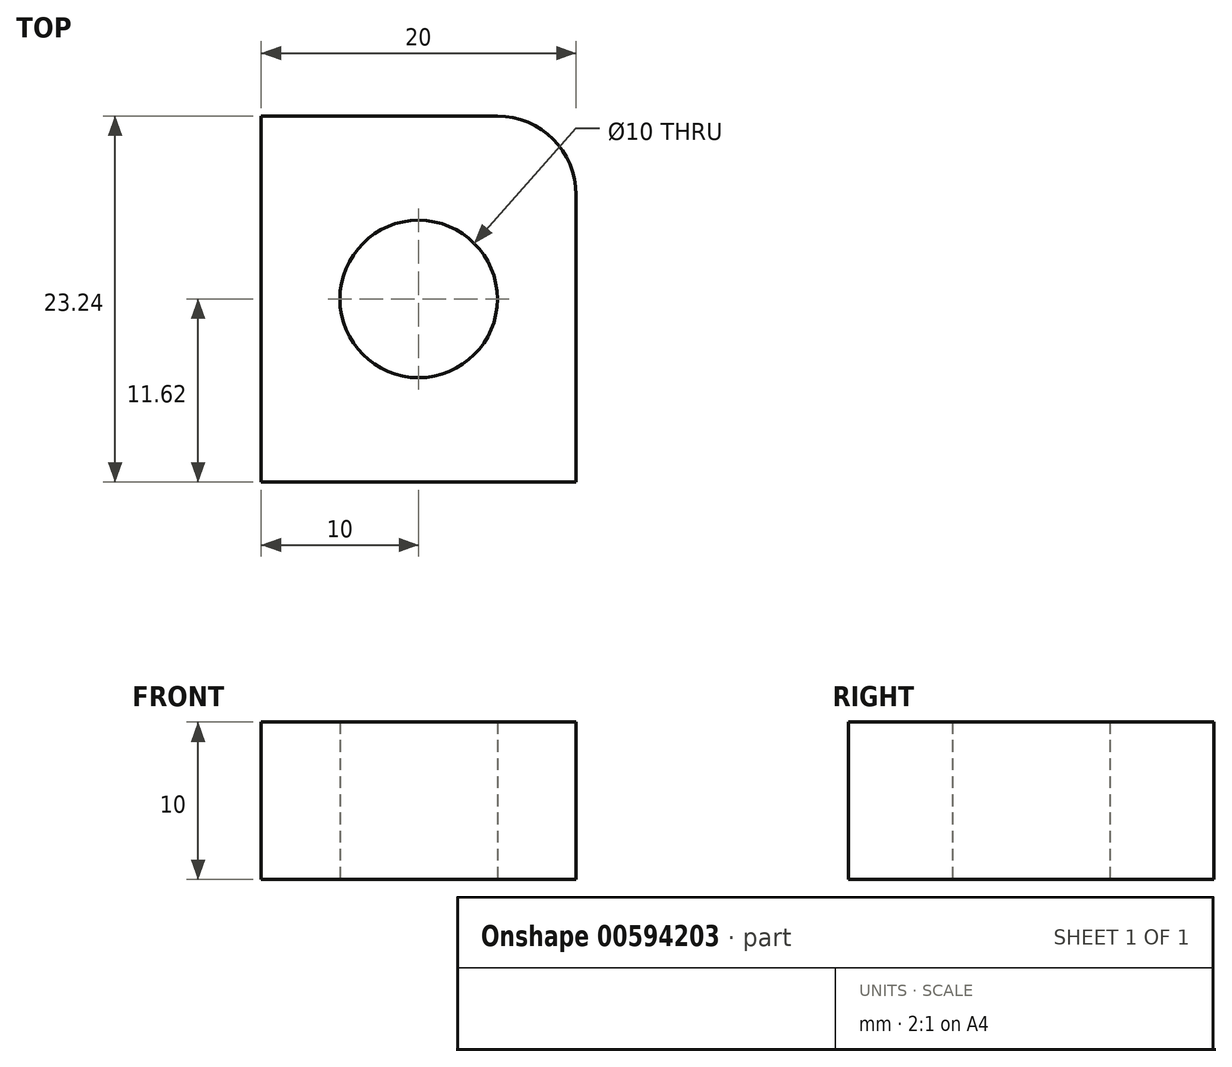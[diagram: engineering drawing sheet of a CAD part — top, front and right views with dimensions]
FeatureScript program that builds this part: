
annotation { "Feature Type Name" : "Feature", "Feature Type Description" : "" }
export const myFeature = defineFeature(function(context is Context, id is Id, definition is map)
    precondition{}
    {
        {
            var Q0;
            Q0=qCreatedBy(makeId("Top.planeOp"),FACE);
            var sketch = newSketch(context, id + "F0", { "sketchPlane" : qUnion([Q0])});
            skLineSegment(sketch, "E0.bottom", {"start": v(10, -11.62) * mm, "end": v(-10, -11.62) * mm});
            skLineSegment(sketch, "E0.top", {"start": v(5, 11.62) * mm, "end": v(-10, 11.62) * mm});
            skLineSegment(sketch, "E0.left", {"start": v(10, -11.62) * mm, "end": v(10, 6.62) * mm});
            skLineSegment(sketch, "E0.right", {"start": v(-10, -11.62) * mm, "end": v(-10, 11.62) * mm});
            skPoint(sketch, "E0.middle", {"position": v(0, 0) * mm});
            skCircle(sketch, "E1", {"center": v(0, 0) * mm, "radius": 5 * mm});
            skPoint(sketch, "E2.visualSharp", {"position": v(10, 11.62) * mm});
            skArc(sketch, "E2.filletArc", {"start": v(10, 6.62) * mm, "mid": v(8.54, 10.15) * mm, "end": v(5, 11.62) * mm});
            skSolve(sketch);
        }
        {
            var Q0;
            Q0=makeQuery(id+"F0.imprint","IMPRINT",FACE,{"disambiguationData":[TD([[makeQuery(id+"F0.imprint","IMPRINT",EDGE,{"derivedFrom":sQuery(id+"F0.wireOp",EDGE,"E0.bottom")}),-1.0]])]});
            extrude(context, id + "F1", {"entities" : qUnion([Q0]), "depth" : 10 * mm, "offsetDistance" : 25 * mm});
        }
    });
